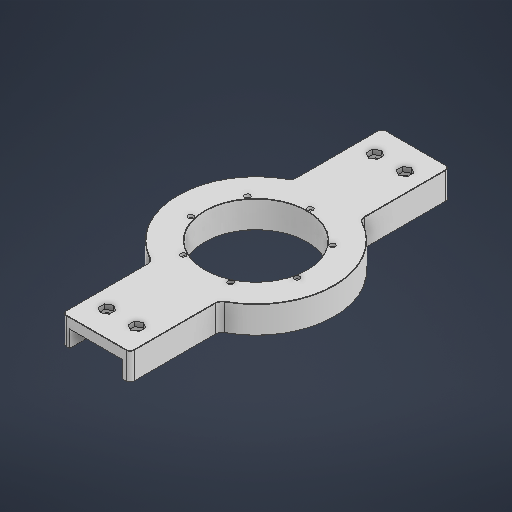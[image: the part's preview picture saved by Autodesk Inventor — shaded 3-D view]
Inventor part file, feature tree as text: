
AUTODESK INVENTOR PART (.ipt)
format: ipt  version: 2025 (Build 290162000, 162)  size: 403,968 bytes
history: native  units: in
note: dims shown in document units (in); Inventor stores cm internally (conversion verified against a paired STEP export)
features: sketch x6, extrude x4, hole x2, fillet x2, chamfer x1
ambient origin geometry x8: Origin, YZ Plane, XZ Plane, XY Plane, X Axis, Y Axis, Z Axis, Center Point
bodies: Solid1 (feature_tree)
feature tree (15):
  extrude  "Extrusion1"  Depth=4.5276in
  sketch  "Sketch2"  dims[d4=0.7874in d5=0.0in d6=3.1496in]
  hole  "Hole1"  [1 undecoded]
  extrude  "Extrusion3"  Depth=0.0787in
  fillet  "Fillet1"  Radius=2.7559in
  fillet  "Fillet2"  Radius=0.0787in
  chamfer  "Chamfer1"  Distance=0.0787in Angle=45.0deg
  extrude  "Extrusion4"  Depth=0.1358in
  hole  "Hole2"  [1 undecoded]
  extrude  "Extrusion5"  Depth=1.5453in
  sketch  "Sketch1"  dims[d0=2.9528in d3=4.5276in]
  sketch  "Sketch Circular Pattern2"  dims[d14=0.0617in d15=0.1575in d16=0.1575in d17=0.0787in d18=90.0deg d19=0.248in d20=0.8108in d21=0.1594in d22=2.7559in d24=360.0deg d26=0.0787in d27=0.0in]
  sketch  "Sketch3"  dims[d28=0.1969in]
  sketch  "Sketch4"  dims[d29=0.1181in d30=0.0098in d31=0.0787in d32=45.0deg]
  sketch  "Sketch5"  dims[d35=1.5453in d37=1.1122in d38=1.1122in d39=1.5453in d40=0.1181in d41=0.1181in d42=0.1181in d43=0.4951in d44=0.0in d45=0.748in d48=0.748in d50=0.0935in d51=0.0935in d52=1.7323in d53=1.5453in d55=0.0935in d56=0.0935in d57=0.748in d58=0.748in d59=0.8661in d60=0.8661in d61=0.3396in d62=0.3396in d63=0.1276in d64=0.315in d65=0.1575in d66=0.0787in d67=90.0deg d68=0.315in d69=0.8108in d70=0.3248in d71=0.3248in d72=0.3248in d73=0.3248in d74=0.1358in d75=0.0in d46=0.0344in]
note: 2 required parameter values undecoded (feature->parameter linkage not recoverable at this tier; creation-order binding heuristic only, values carry confidence <= 0.55)
